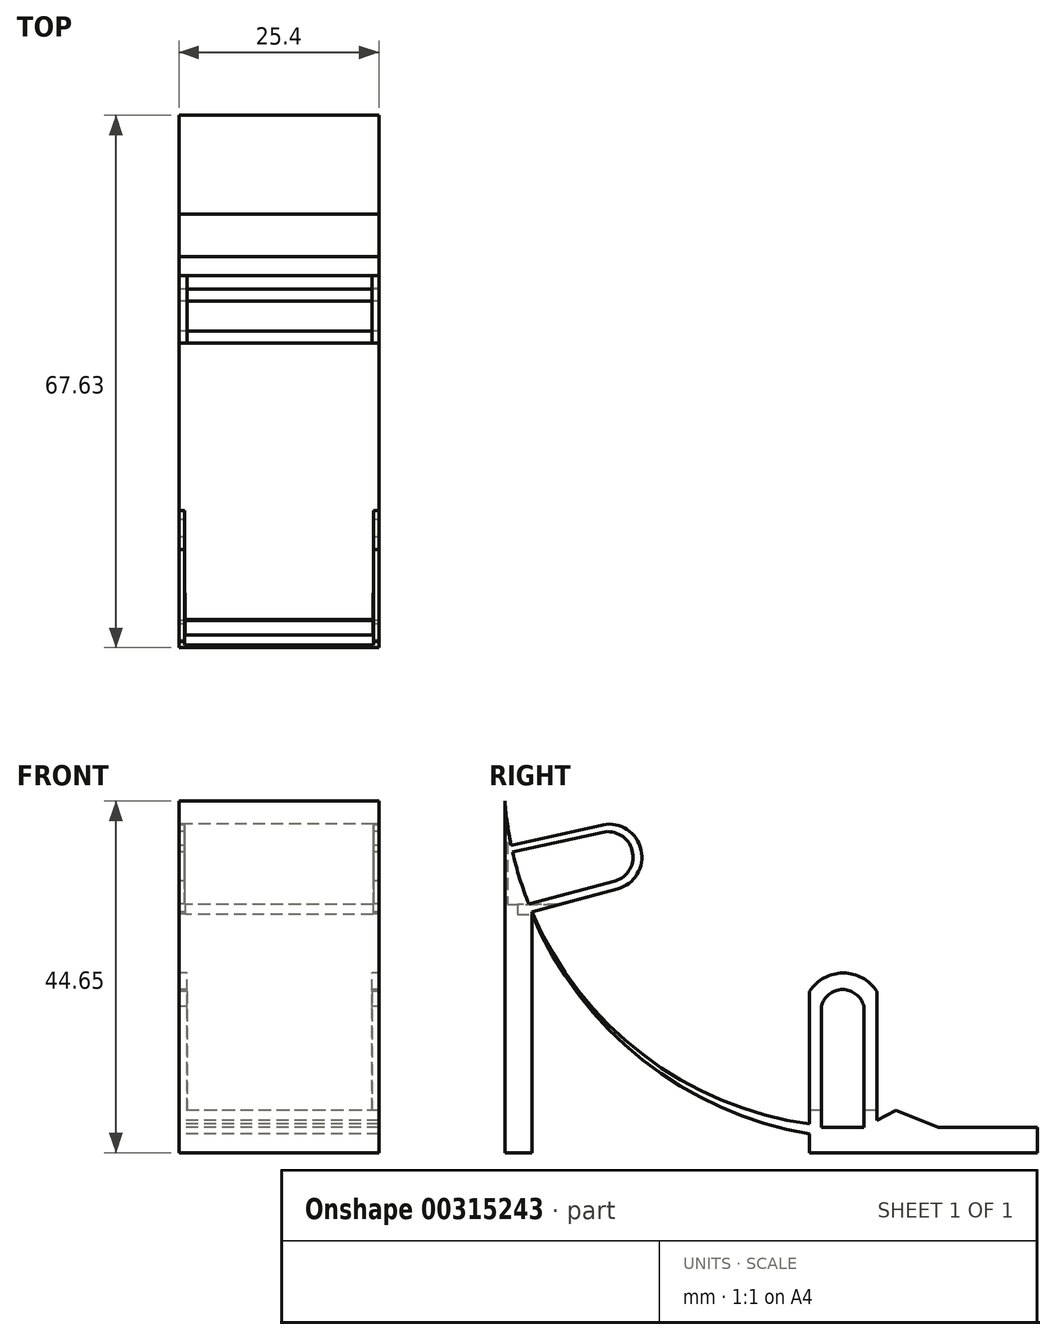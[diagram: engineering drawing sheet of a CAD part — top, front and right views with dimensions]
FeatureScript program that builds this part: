
annotation { "Feature Type Name" : "Feature", "Feature Type Description" : "" }
export const myFeature = defineFeature(function(context is Context, id is Id, definition is map)
    precondition{}
    {
        {
            var Q0;
            Q0=qCreatedBy(makeId("Right.planeOp"),FACE);
            var sketch = newSketch(context, id + "F0", { "sketchPlane" : qUnion([Q0])});
            skLineSegment(sketch, "E0.bottom", {"start": v(0, 3.22) * mm, "end": v(-28.9, 3.22) * mm});
            skLineSegment(sketch, "E0.top", {"start": v(0, 0) * mm, "end": v(-28.9, 0) * mm});
            skLineSegment(sketch, "E0.left", {"start": v(0, 3.22) * mm, "end": v(0, 0) * mm});
            skLineSegment(sketch, "E0.right", {"start": v(-28.9, 3.22) * mm, "end": v(-28.9, 0) * mm});
            skArc(sketch, "E1", {"start": v(-67.63, 44.65) * mm, "mid": v(-53.03, 14.9) * mm, "end": v(-22.02, 3.22) * mm});
            skLineSegment(sketch, "E2", {"start": v(-28.9, 0) * mm, "end": v(-28.9, 20.5) * mm});
            skLineSegment(sketch, "E3", {"start": v(-20.4, 20.5) * mm, "end": v(-20.4, 0) * mm});
            skArc(sketch, "E4", {"start": v(-20.4, 20.5) * mm, "mid": v(-24.65, 22.82) * mm, "end": v(-28.9, 20.5) * mm});
            skLineSegment(sketch, "E5", {"start": v(-66.31, 36.83) * mm, "end": v(-63.3, 36.83) * mm});
            skLineSegment(sketch, "E6", {"start": v(-63.3, 36.83) * mm, "end": v(-64.2, 30.6) * mm});
            skLineSegment(sketch, "E7", {"start": v(-12.56, 3.22) * mm, "end": v(-17.97, 5.36) * mm});
            skLineSegment(sketch, "E8", {"start": v(-17.97, 5.36) * mm, "end": v(-22.02, 3.22) * mm});
            skLineSegment(sketch, "E9", {"start": v(-66.83, 39.02) * mm, "end": v(-55.18, 41.66) * mm});
            skLineSegment(sketch, "E10", {"start": v(-53.33, 33.5) * mm, "end": v(-64.2, 30.6) * mm});
            skArc(sketch, "E11", {"start": v(-53.33, 33.5) * mm, "mid": v(-50.32, 38.47) * mm, "end": v(-55.18, 41.66) * mm});
            skLineSegment(sketch, "E12", {"start": v(-64.2, 30.6) * mm, "end": v(-64.2, 0) * mm});
            skLineSegment(sketch, "E13", {"start": v(-67.63, 44.65) * mm, "end": v(-67.63, 0) * mm});
            skLineSegment(sketch, "E14", {"start": v(-67.63, 0) * mm, "end": v(-64.2, 0) * mm});
            skLineSegment(sketch, "E15", {"start": v(-64.6, 31.58) * mm, "end": v(-53.6, 34.5) * mm});
            skLineSegment(sketch, "E16", {"start": v(-55.24, 40.7) * mm, "end": v(-66.65, 38.2) * mm});
            skArc(sketch, "E17", {"start": v(-53.6, 34.5) * mm, "mid": v(-51.45, 38.4) * mm, "end": v(-55.24, 40.7) * mm});
            skLineSegment(sketch, "E18", {"start": v(-27.4, 3.22) * mm, "end": v(-27.4, 18.59) * mm});
            skLineSegment(sketch, "E19", {"start": v(-22.05, 18.59) * mm, "end": v(-22.05, 3.22) * mm});
            skArc(sketch, "E20", {"start": v(-22.05, 18.59) * mm, "mid": v(-24.72, 20.72) * mm, "end": v(-27.4, 18.59) * mm});
            skArc(sketch, "E21.0", {"start": v(-67.63, 44.65) * mm, "mid": v(-53.13, 14.36) * mm, "end": v(-22, 1.78) * mm});
            skLineSegment(sketch, "E22.bottom", {"start": v(-28.9, 3.22) * mm, "end": v(-20.4, 3.22) * mm});
            skLineSegment(sketch, "E22.top", {"start": v(-28.9, 0) * mm, "end": v(-20.4, 0) * mm});
            skLineSegment(sketch, "E22.right", {"start": v(-20.4, 3.22) * mm, "end": v(-20.4, 0) * mm});
            skSolve(sketch);
        }
        {
            var Q0;
            Q0 = qSketchRegion(id + "F0", true);
            extrude(context, id + "F1", {"entities" : qUnion([Q0]), "depth" : 25.4 * mm});
        }
        {
            var Q0;
            Q0=qCreatedBy(makeId("Front.planeOp"),FACE);
            var sketch = newSketch(context, id + "F2", { "sketchPlane" : qUnion([Q0])});
            skLineSegment(sketch, "E23.bottom", {"start": v(24.71, 42.47) * mm, "end": v(0.72, 42.47) * mm});
            skLineSegment(sketch, "E23.top", {"start": v(24.71, 31.54) * mm, "end": v(0.72, 31.54) * mm});
            skLineSegment(sketch, "E23.left", {"start": v(24.71, 42.47) * mm, "end": v(24.71, 31.54) * mm});
            skLineSegment(sketch, "E23.right", {"start": v(0.72, 42.47) * mm, "end": v(0.72, 31.54) * mm});
            skSolve(sketch);
        }
        {
            var Q0;
            Q0 = qSketchRegion(id + "F2", true);
            extrude(context, id + "F3", {"entities" : qUnion([Q0]), "operationType" : NewBodyOperationType.REMOVE, "depth" : 63.5 * mm});
        }
        {
            var Q0;
            Q0 = qSketchRegion(id + "F2", true);
            extrude(context, id + "F4", {"entities" : qUnion([Q0]), "operationType" : NewBodyOperationType.REMOVE, "depth" : 67.3 * mm});
        }
        {
            var Q0;
            Q0=qCreatedBy(makeId("Front.planeOp"),FACE);
            var sketch = newSketch(context, id + "F5", { "sketchPlane" : qUnion([Q0])});
            skLineSegment(sketch, "E24.bottom", {"start": v(24.63, 32.73) * mm, "end": v(0.8, 32.73) * mm});
            skLineSegment(sketch, "E24.top", {"start": v(24.63, 30.28) * mm, "end": v(0.8, 30.28) * mm});
            skLineSegment(sketch, "E24.left", {"start": v(24.63, 32.73) * mm, "end": v(24.63, 30.28) * mm});
            skLineSegment(sketch, "E24.right", {"start": v(0.8, 32.73) * mm, "end": v(0.8, 30.28) * mm});
            skSolve(sketch);
        }
        {
            var Q0;
            Q0 = qSketchRegion(id + "F5", true);
            extrude(context, id + "F6", {"entities" : qUnion([Q0]), "operationType" : NewBodyOperationType.REMOVE, "depth" : 66.04 * mm});
        }
        {
            var Q0;
            Q0=qCreatedBy(makeId("Front.planeOp"),FACE);
            var sketch = newSketch(context, id + "F7", { "sketchPlane" : qUnion([Q0])});
            skLineSegment(sketch, "E25.bottom", {"start": v(24.5, 23.32) * mm, "end": v(1.03, 23.32) * mm});
            skLineSegment(sketch, "E25.top", {"start": v(24.5, 5.46) * mm, "end": v(1.03, 5.46) * mm});
            skLineSegment(sketch, "E25.left", {"start": v(24.5, 23.32) * mm, "end": v(24.5, 5.46) * mm});
            skLineSegment(sketch, "E25.right", {"start": v(1.03, 23.32) * mm, "end": v(1.03, 5.46) * mm});
            skSolve(sketch);
        }
        {
            var Q0;
            Q0 = qSketchRegion(id + "F7", true);
            extrude(context, id + "F8", {"entities" : qUnion([Q0]), "operationType" : NewBodyOperationType.REMOVE, "depth" : 34.3 * mm});
        }
        {
            var Q0;
            Q0=sQuery(id+"F0.wireOp",EDGE,"E1");
            extrude(context, id + "F9", {"bodyType" : ToolBodyType.SURFACE, "surfaceEntities" : qUnion([Q0]), "depth" : 25.4 * mm});
        }
        {
            var Q0;
            Q0=sQuery(id+"F0.wireOp",EDGE,"E21.0");
            extrude(context, id + "F10", {"bodyType" : ToolBodyType.SURFACE, "surfaceEntities" : qUnion([Q0]), "depth" : 25.4 * mm});
        }
    });
